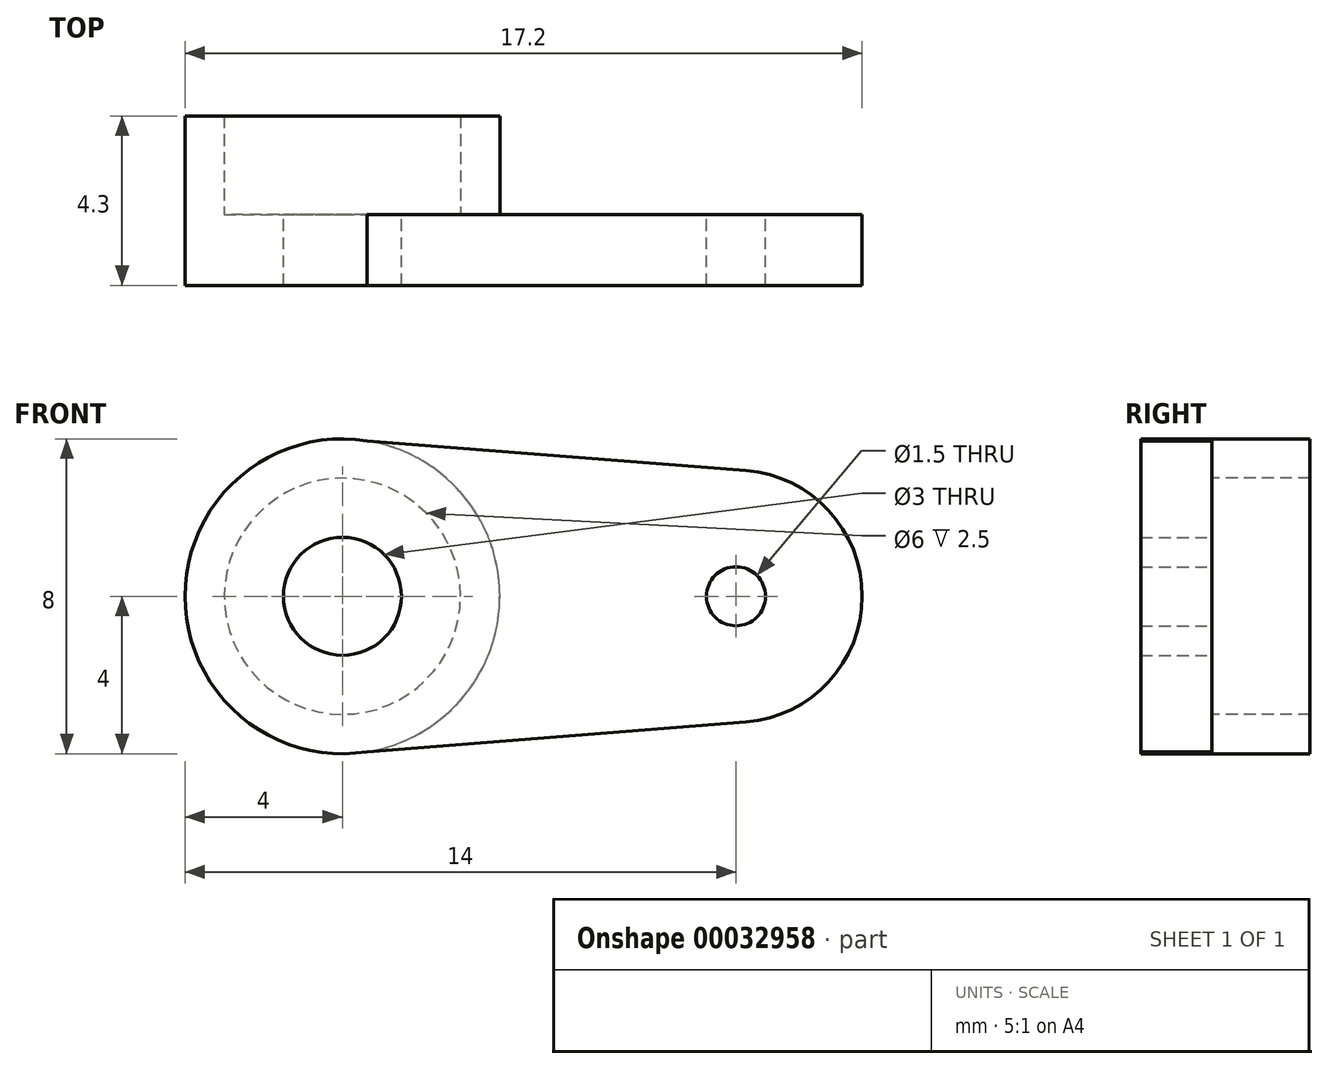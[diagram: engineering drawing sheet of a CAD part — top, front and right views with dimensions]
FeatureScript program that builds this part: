
annotation { "Feature Type Name" : "Feature", "Feature Type Description" : "" }
export const myFeature = defineFeature(function(context is Context, id is Id, definition is map)
    precondition{}
    {
        {
            var Q0;
            Q0=qCreatedBy(makeId("Front.planeOp"),FACE);
            var sketch = newSketch(context, id + "F0", { "sketchPlane" : qUnion([Q0])});
            skArc(sketch, "E0", {"start": v(0.62, 3.95) * mm, "mid": v(-4, 0) * mm, "end": v(0.62, -3.95) * mm});
            skLineSegment(sketch, "E1", {"start": v(0, 4) * mm, "end": v(10.25, 3.2) * mm});
            skLineSegment(sketch, "E2.MirrorCS", {"start": v(0, -4) * mm, "end": v(10.25, -3.2) * mm});
            skCircle(sketch, "E3", {"center": v(0, 0) * mm, "radius": 1.5 * mm});
            skCircle(sketch, "E4.3.0.0", {"center": v(10, 0) * mm, "radius": 0.75 * mm});
            skArc(sketch, "E5", {"start": v(10.25, -3.2) * mm, "mid": v(13.2, 0) * mm, "end": v(10.25, 3.2) * mm});
            skSolve(sketch);
        }
        {
            var Q0;
            Q0 = qSketchRegion(id + "F0", true);
            extrude(context, id + "F1", {"entities" : qUnion([Q0]), "depth" : 1.8 * mm});
        }
        {
            var Q0;
            Q0=makeQuery(id+"F1.opExtrude","CAP_FACE",FACE,{"disambiguationData":[OSD([sQuery(id+"F0.wireOp",EDGE,"E0"),sQuery(id+"F0.wireOp",EDGE,"028a310e-2503-4363-b4da-8f641bdb4973"),sQuery(id+"F0.wireOp",EDGE,"E1"),sQuery(id+"F0.wireOp",EDGE,"E2.MirrorCS"),sQuery(id+"F0.wireOp",EDGE,"E3"),sQuery(id+"F0.wireOp",EDGE,"cb723fb1-20d7-435c-80aa-65bd687a6050"),sQuery(id+"F0.wireOp",EDGE,"E4.1.0.0"),sQuery(id+"F0.wireOp",EDGE,"E4.2.0.0"),sQuery(id+"F0.wireOp",EDGE,"E4.3.0.0")])],"isStart":true});
            var sketch = newSketch(context, id + "F2", { "sketchPlane" : qUnion([Q0])});
            skCircle(sketch, "E6", {"center": v(0, 0) * mm, "radius": 4 * mm});
            skCircle(sketch, "E7", {"center": v(0, 0) * mm, "radius": 3 * mm});
            skSolve(sketch);
        }
        {
            var Q0;
            Q0 = qSketchRegion(id + "F2", true);
            extrude(context, id + "F3", {"entities" : qUnion([Q0]), "operationType" : NewBodyOperationType.ADD, "depth" : 2.5 * mm});
        }
    });
